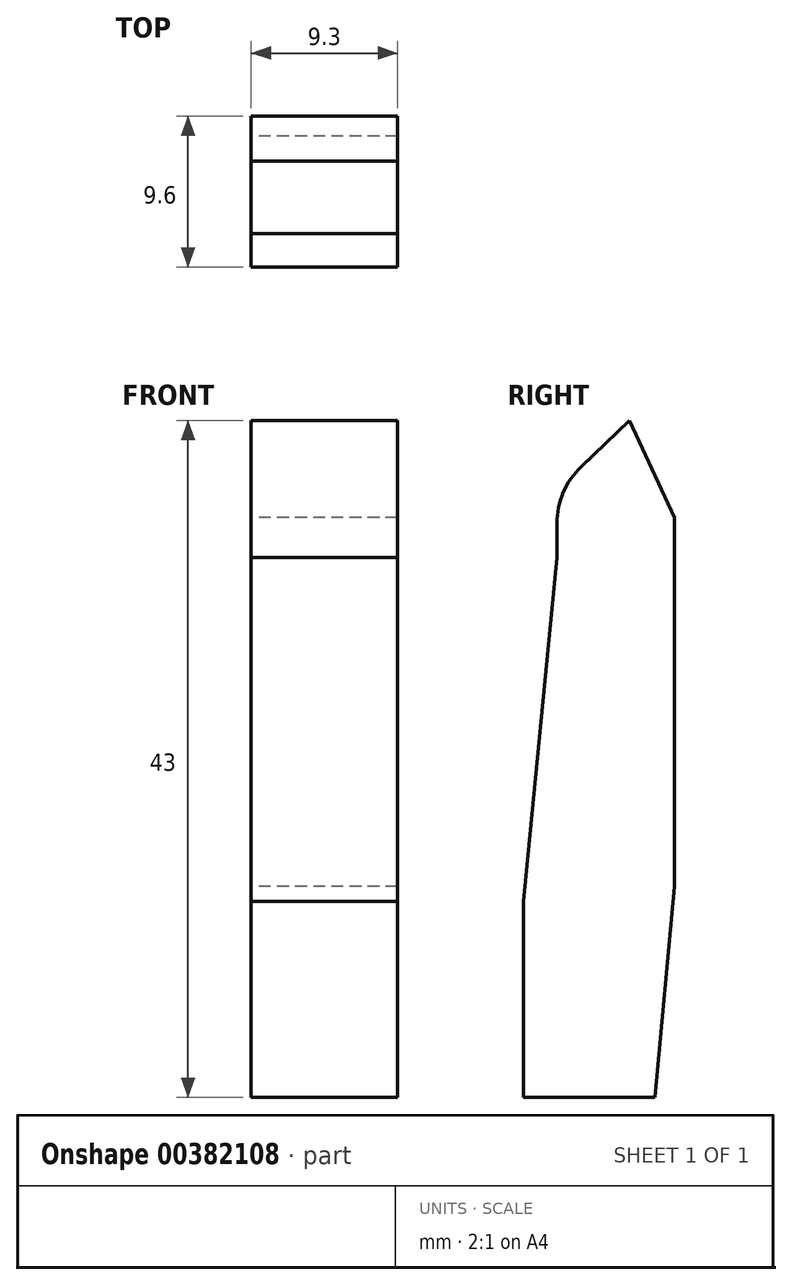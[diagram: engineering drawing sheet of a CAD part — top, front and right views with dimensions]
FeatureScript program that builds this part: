
annotation { "Feature Type Name" : "Feature", "Feature Type Description" : "" }
export const myFeature = defineFeature(function(context is Context, id is Id, definition is map)
    precondition{}
    {
        {
            var Q0;
            Q0=qCreatedBy(makeId("Top.planeOp"),FACE);
            var sketch = newSketch(context, id + "F0", { "sketchPlane" : qUnion([Q0])});
            skLineSegment(sketch, "E0.bottom", {"start": v(-59.1, 58.65) * mm, "end": v(-49.8, 58.65) * mm});
            skLineSegment(sketch, "E0.top", {"start": v(-59.1, 49.05) * mm, "end": v(-49.8, 49.05) * mm});
            skLineSegment(sketch, "E0.left", {"start": v(-59.1, 58.65) * mm, "end": v(-59.1, 49.05) * mm});
            skLineSegment(sketch, "E0.right", {"start": v(-49.8, 58.65) * mm, "end": v(-49.8, 49.05) * mm});
            skSolve(sketch);
        }
        {
            var Q0;
            Q0=makeQuery(id+"F0.imprint","IMPRINT",FACE,{"disambiguationData":[TD([[makeQuery(id+"F0.imprint","IMPRINT",EDGE,{"derivedFrom":sQuery(id+"F0.wireOp",EDGE,"E0.bottom")}),-1.0]])]});
            extrude(context, id + "F1", {"entities" : qUnion([Q0]), "depth" : 43 * mm});
        }
        {
            var Q0;
            Q0=makeQuery(id+"F1.opExtrude","SWEPT_FACE",FACE,{"disambiguationData":[OSD([sQuery(id+"F0.wireOp",EDGE,"E0.left")])]});
            var sketch = newSketch(context, id + "F2", { "sketchPlane" : qUnion([Q0])});
            skLineSegment(sketch, "E1", {"start": v(-55.79, 43) * mm, "end": v(-58.65, 36.85) * mm});
            skLineSegment(sketch, "E2", {"start": v(-58.65, 36.85) * mm, "end": v(-58.65, 13.42) * mm});
            skLineSegment(sketch, "E3", {"start": v(-58.65, 13.42) * mm, "end": v(-57.38, 0) * mm});
            skLineSegment(sketch, "E4", {"start": v(-57.38, 0) * mm, "end": v(-49.05, 0) * mm});
            skLineSegment(sketch, "E5", {"start": v(-49.05, 0) * mm, "end": v(-49.05, 12.47) * mm});
            skLineSegment(sketch, "E6", {"start": v(-49.05, 12.47) * mm, "end": v(-51.17, 34.3) * mm});
            skLineSegment(sketch, "E7", {"start": v(-51.17, 34.3) * mm, "end": v(-51.17, 38.6) * mm});
            skLineSegment(sketch, "E8", {"start": v(-51.17, 38.6) * mm, "end": v(-55.79, 43) * mm});
            skSolve(sketch);
        }
        {
            var Q0;
            {var subQ4=sQuery(id+"F2.wireOp",EDGE,"E6");Q0=makeQuery(id+"F2.imprint","IMPRINT",FACE,{"disambiguationData":[TD([[makeQuery(id+"F2.imprint","IMPRINT",EDGE,{"derivedFrom":subQ4}),-1.0]])]});}
            var Q1;
            {var subQ0=sQuery(id+"F2.wireOp",EDGE,"E1");Q1=makeQuery(id+"F2.imprint","IMPRINT",FACE,{"disambiguationData":[TD([[makeQuery(id+"F2.imprint","IMPRINT",EDGE,{"derivedFrom":subQ0}),-1.0]])]});}
            var Q2;
            {var subQ0=sQuery(id+"F2.wireOp",EDGE,"E3");Q2=makeQuery(id+"F2.imprint","IMPRINT",FACE,{"disambiguationData":[TD([[makeQuery(id+"F2.imprint","IMPRINT",EDGE,{"derivedFrom":subQ0}),-1.0]])]});}
            extrude(context, id + "F3", {"entities" : qUnion([Q0, Q1, Q2]), "operationType" : NewBodyOperationType.REMOVE, "endBound" : BoundingType.THROUGH_ALL, "oppositeDirection" : true, "depth" : 25 * mm});
        }
        {
            var Q0;
            Q0=makeQuery(id+"F3.boolean.opBoolean","COPY",EDGE,{"derivedFrom":makeQuery(id+"F3.opExtrude","SWEPT_EDGE",EDGE,{"disambiguationData":[OSD([sQuery(id+"F2.wireOp",EDGE,"E7"),sQuery(id+"F2.wireOp",EDGE,"E8")])]})});
            var Q1;
            Q1=makeQuery(id+"F3.boolean.opBoolean","COPY",EDGE,{"derivedFrom":makeQuery(id+"F3.opExtrude","SWEPT_EDGE",EDGE,{"disambiguationData":[OSD([sQuery(id+"F0.wireOp",EDGE,"E0.bottom"),sQuery(id+"F0.wireOp",EDGE,"E0.left"),sQuery(id+"F2.wireOp",EDGE,"E1"),sQuery(id+"F2.wireOp",EDGE,"E2")])]})});
            fillet(context, id + "F4", {"entities" : qUnion([Q0, Q1]), "radius" : 5 * mm, "tangentPropagation" : true, "allowEdgeOverflow" : false});
        }
    });
